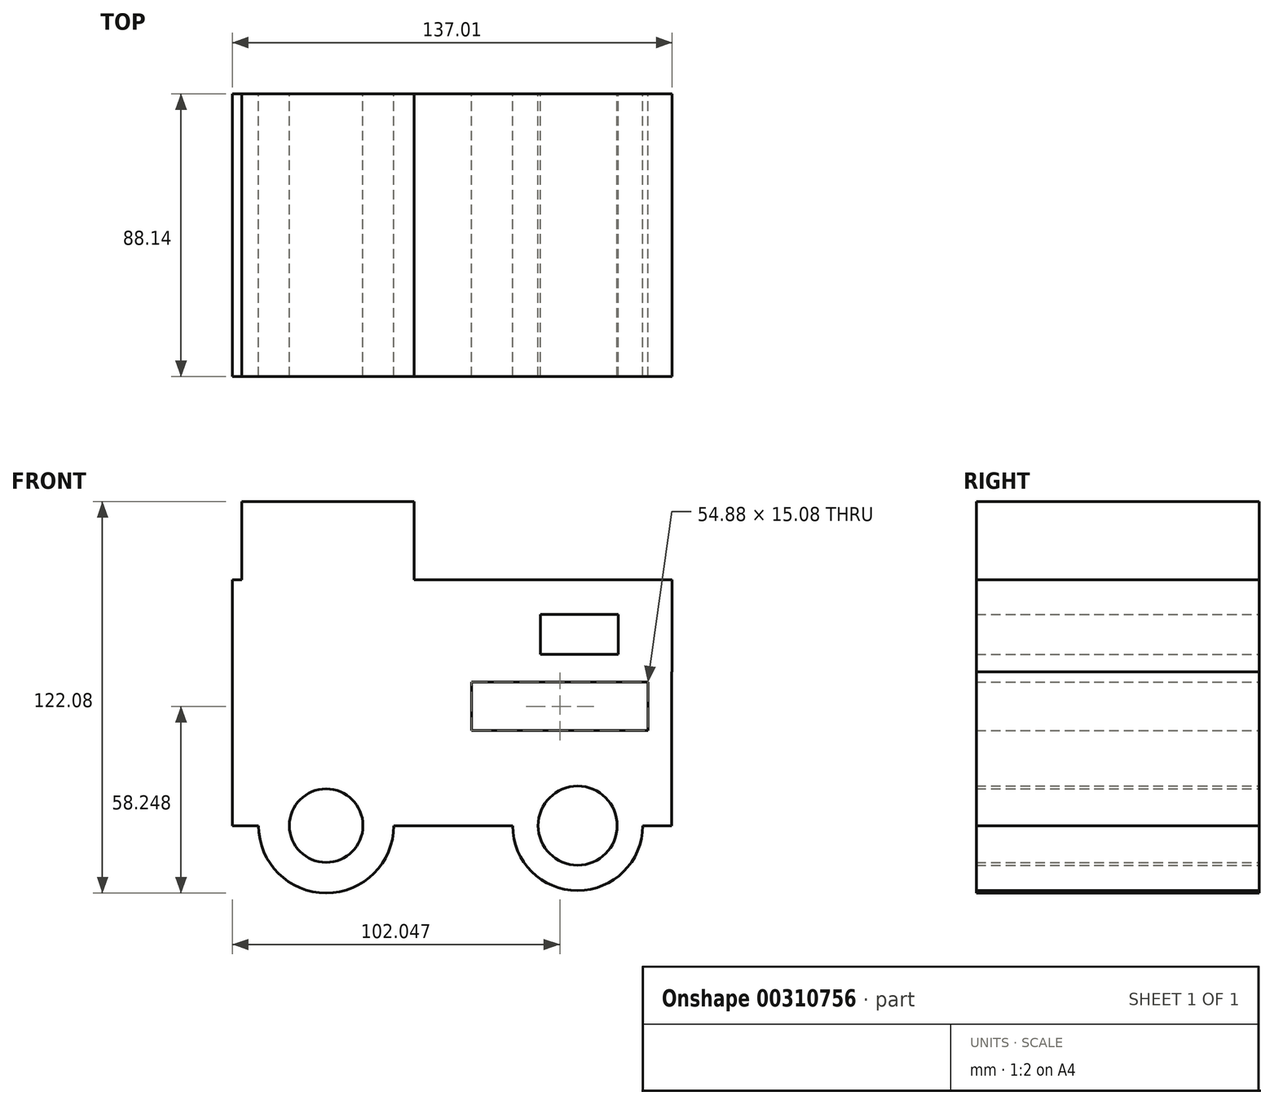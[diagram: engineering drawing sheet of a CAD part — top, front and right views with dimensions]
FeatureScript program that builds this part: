
annotation { "Feature Type Name" : "Feature", "Feature Type Description" : "" }
export const myFeature = defineFeature(function(context is Context, id is Id, definition is map)
    precondition{}
    {
        {
            var Q0;
            Q0=qCreatedBy(makeId("Front.planeOp"),FACE);
            var sketch = newSketch(context, id + "F0", { "sketchPlane" : qUnion([Q0])});
            skLineSegment(sketch, "E0.bottom", {"start": v(-61.03, 18.33) * mm, "end": v(75.89, 18.33) * mm});
            skLineSegment(sketch, "E0.top", {"start": v(-61.03, -29.65) * mm, "end": v(75.89, -29.65) * mm});
            skLineSegment(sketch, "E0.left", {"start": v(-61.03, 18.33) * mm, "end": v(-61.03, -29.65) * mm});
            skLineSegment(sketch, "E0.right", {"start": v(75.89, 18.33) * mm, "end": v(75.89, -29.65) * mm});
            skCircle(sketch, "E1", {"center": v(-31.82, -29.65) * mm, "radius": 21.06 * mm});
            skCircle(sketch, "E2", {"center": v(46.57, -29.65) * mm, "radius": 20.26 * mm});
            skLineSegment(sketch, "E3.bottom", {"start": v(-61.03, 18.33) * mm, "end": v(75.98, 18.33) * mm});
            skLineSegment(sketch, "E3.top", {"start": v(-61.03, 47.01) * mm, "end": v(75.98, 47.01) * mm});
            skLineSegment(sketch, "E3.left", {"start": v(-61.03, 18.33) * mm, "end": v(-61.03, 47.01) * mm});
            skLineSegment(sketch, "E3.right", {"start": v(75.98, 18.33) * mm, "end": v(75.98, 47.01) * mm});
            skCircle(sketch, "E4", {"center": v(46.57, -29.65) * mm, "radius": 12.33 * mm});
            skCircle(sketch, "E5", {"center": v(-31.82, -29.65) * mm, "radius": 11.47 * mm});
            skLineSegment(sketch, "E6.bottom", {"start": v(-22.03, 36.19) * mm, "end": v(-43.72, 36.19) * mm});
            skLineSegment(sketch, "E6.top", {"start": v(-22.03, 23.75) * mm, "end": v(-43.72, 23.75) * mm});
            skLineSegment(sketch, "E6.left", {"start": v(-22.03, 36.19) * mm, "end": v(-22.03, 23.75) * mm});
            skLineSegment(sketch, "E6.right", {"start": v(-43.72, 36.19) * mm, "end": v(-43.72, 23.75) * mm});
            skPoint(sketch, "E7.oppositeSnap0", {"position": v(-32.87, 23.75) * mm});
            skLineSegment(sketch, "E7.bottom", {"start": v(34.95, 36.19) * mm, "end": v(59.25, 36.19) * mm});
            skLineSegment(sketch, "E7.top", {"start": v(34.95, 23.75) * mm, "end": v(59.25, 23.75) * mm});
            skLineSegment(sketch, "E7.left", {"start": v(34.95, 36.19) * mm, "end": v(34.95, 23.75) * mm});
            skLineSegment(sketch, "E7.right", {"start": v(59.25, 36.19) * mm, "end": v(59.25, 23.75) * mm});
            skLineSegment(sketch, "E8.bottom", {"start": v(68.46, 15.08) * mm, "end": v(13.57, 15.08) * mm});
            skLineSegment(sketch, "E8.top", {"start": v(68.46, 0) * mm, "end": v(13.57, 0) * mm});
            skLineSegment(sketch, "E8.left", {"start": v(68.46, 15.08) * mm, "end": v(68.46, 0) * mm});
            skLineSegment(sketch, "E8.right", {"start": v(13.57, 15.08) * mm, "end": v(13.57, 0) * mm});
            skLineSegment(sketch, "E9.bottom", {"start": v(-4.42, 15.38) * mm, "end": v(-58.08, 15.38) * mm});
            skLineSegment(sketch, "E9.top", {"start": v(-4.42, 0) * mm, "end": v(-58.08, 0) * mm});
            skLineSegment(sketch, "E9.left", {"start": v(-4.42, 15.38) * mm, "end": v(-4.42, 0) * mm});
            skLineSegment(sketch, "E9.right", {"start": v(-58.08, 15.38) * mm, "end": v(-58.08, 0) * mm});
            skSolve(sketch);
        }
        {
            var Q0;
            Q0 = qSketchRegion(id + "F0", true);
            extrude(context, id + "F1", {"entities" : qUnion([Q0]), "depth" : 25.4 * mm});
        }
        {
            var Q0;
            Q0=makeQuery(id+"F1.opExtrude","CAP_FACE",FACE,{"disambiguationData":[OSD([sQuery(id+"F0.wireOp",EDGE,"E0.top"),sQuery(id+"F0.wireOp",EDGE,"E0.left"),sQuery(id+"F0.wireOp",EDGE,"E0.right"),sQuery(id+"F0.wireOp",EDGE,"E1"),sQuery(id+"F0.wireOp",EDGE,"E2"),sQuery(id+"F0.wireOp",EDGE,"E3.bottom"),sQuery(id+"F0.wireOp",EDGE,"E3.top"),sQuery(id+"F0.wireOp",EDGE,"E3.left"),sQuery(id+"F0.wireOp",EDGE,"E3.right"),sQuery(id+"F0.wireOp",EDGE,"E4"),sQuery(id+"F0.wireOp",EDGE,"E5"),sQuery(id+"F0.wireOp",EDGE,"E6.bottom"),sQuery(id+"F0.wireOp",EDGE,"E6.top"),sQuery(id+"F0.wireOp",EDGE,"E6.left"),sQuery(id+"F0.wireOp",EDGE,"E6.right"),sQuery(id+"F0.wireOp",EDGE,"E7.bottom"),sQuery(id+"F0.wireOp",EDGE,"E7.top"),sQuery(id+"F0.wireOp",EDGE,"E7.left"),sQuery(id+"F0.wireOp",EDGE,"E7.right")])],"isStart":true});
            extrude(context, id + "F2", {"entities" : qUnion([Q0]), "operationType" : NewBodyOperationType.ADD, "depth" : 62.74 * mm});
        }
        {
            var Q0;
            {var subQ0=sQuery(id+"F0.wireOp",EDGE,"E9.top");Q0=makeQuery(id+"F2.boolean.opBoolean","MERGE",FACE,{"derivedFrom":[makeQuery(id+"F1.opExtrude","SWEPT_FACE",FACE,{"disambiguationData":[OSD([subQ0])]}),makeQuery(id+"F2.opExtrude","SWEPT_FACE",FACE,{"disambiguationData":[OSD([subQ0])]})]});}
            extrude(context, id + "F3", {"entities" : qUnion([Q0]), "operationType" : NewBodyOperationType.ADD, "depth" : 71.37 * mm});
        }
    });
